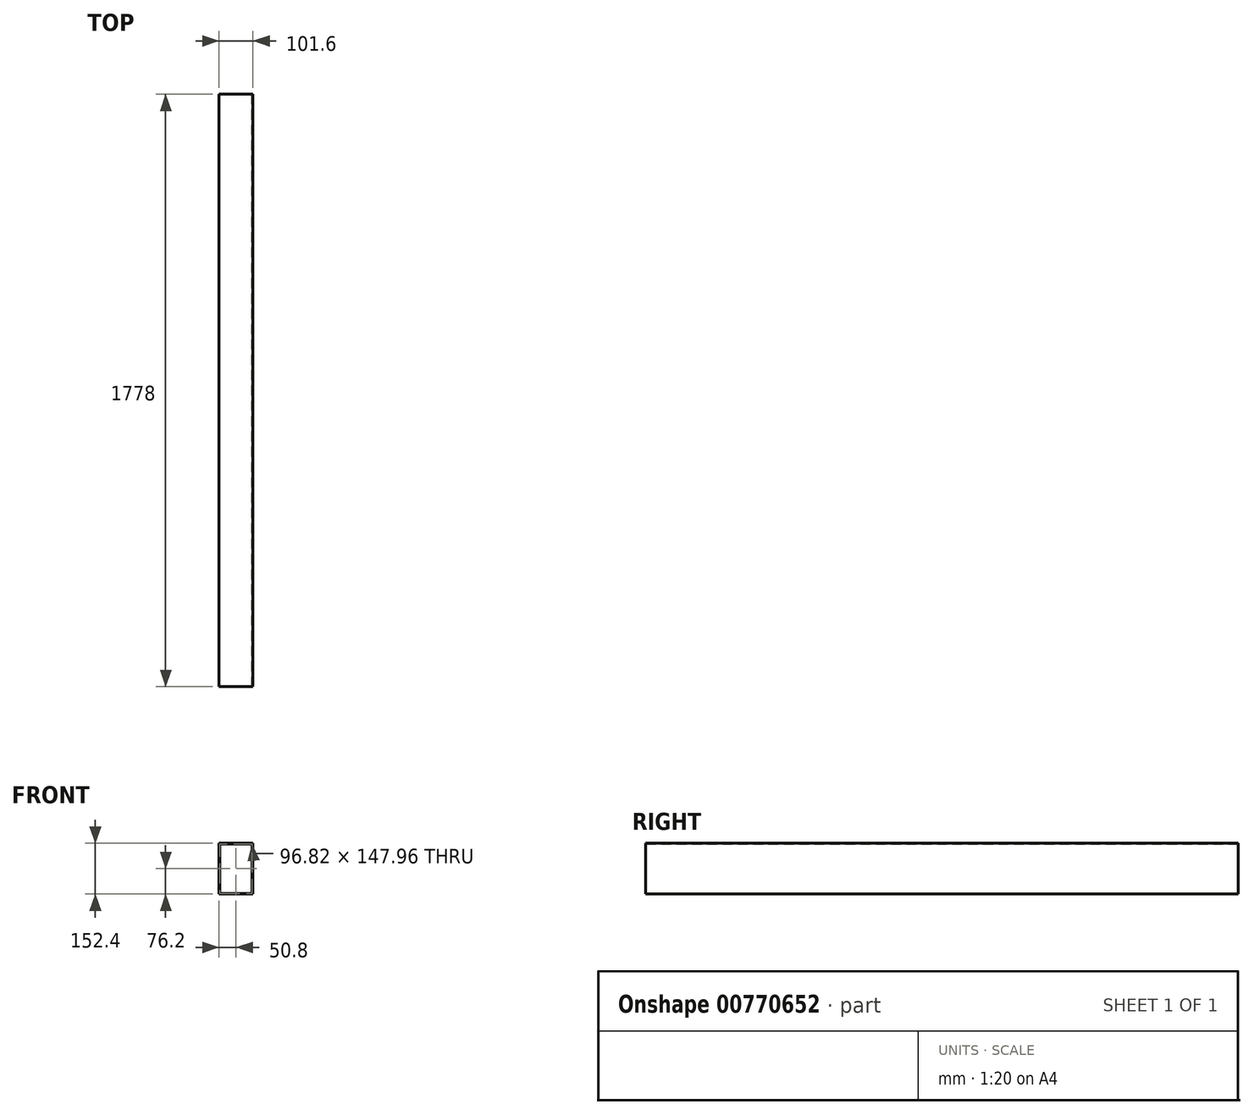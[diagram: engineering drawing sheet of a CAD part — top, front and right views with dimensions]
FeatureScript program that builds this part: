
annotation { "Feature Type Name" : "Feature", "Feature Type Description" : "" }
export const myFeature = defineFeature(function(context is Context, id is Id, definition is map)
    precondition{}
    {
        {
            var Q0;
            Q0=qCreatedBy(makeId("Front.planeOp"),FACE);
            var sketch = newSketch(context, id + "F0", { "sketchPlane" : qUnion([Q0])});
            skLineSegment(sketch, "E0.bottom", {"start": v(50.8, -76.2) * mm, "end": v(-50.8, -76.2) * mm});
            skLineSegment(sketch, "E0.top", {"start": v(50.8, 76.2) * mm, "end": v(-50.8, 76.2) * mm});
            skLineSegment(sketch, "E0.left", {"start": v(50.8, -76.2) * mm, "end": v(50.8, 76.2) * mm});
            skLineSegment(sketch, "E0.right", {"start": v(-50.8, -76.2) * mm, "end": v(-50.8, 76.2) * mm});
            skPoint(sketch, "E0.middle", {"position": v(0, 0) * mm});
            skLineSegment(sketch, "E1.bottom", {"start": v(48.41, -73.98) * mm, "end": v(-48.41, -73.98) * mm});
            skLineSegment(sketch, "E1.top", {"start": v(48.41, 73.98) * mm, "end": v(-48.41, 73.98) * mm});
            skLineSegment(sketch, "E1.left", {"start": v(48.41, -73.98) * mm, "end": v(48.41, 73.98) * mm});
            skLineSegment(sketch, "E1.right", {"start": v(-48.41, -73.98) * mm, "end": v(-48.41, 73.98) * mm});
            skSolve(sketch);
        }
        {
            var Q0;
            Q0=qSketchRegion(id+"F0",true);
            extrude(context, id + "F1", {"entities" : qUnion([Q0]), "depth" : 1778 * mm, "offsetDistance" : 25.4 * mm});
        }
    });
